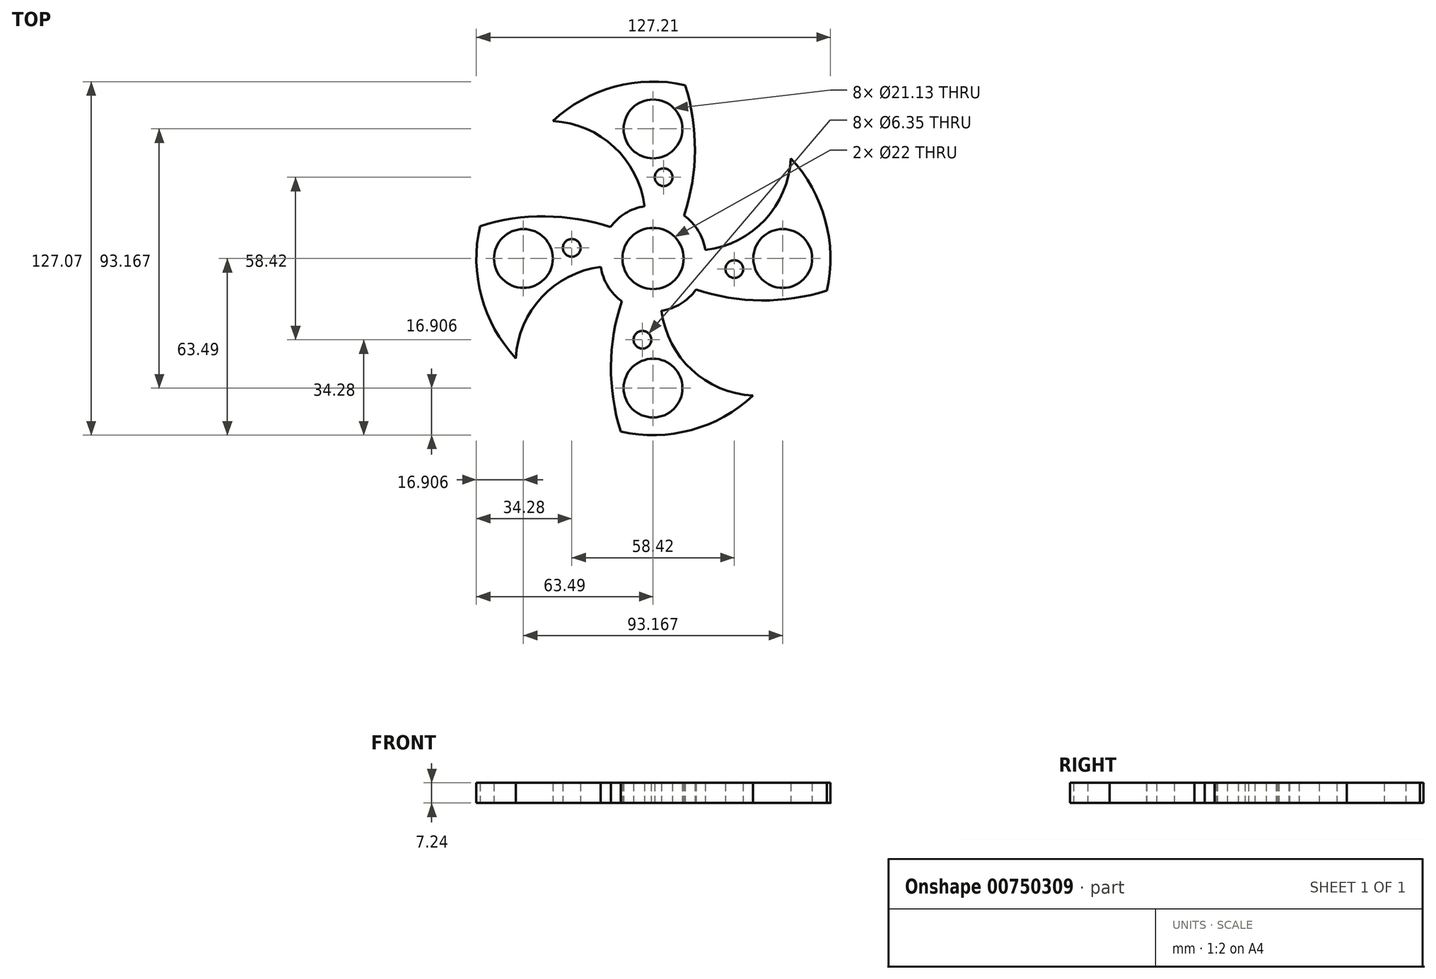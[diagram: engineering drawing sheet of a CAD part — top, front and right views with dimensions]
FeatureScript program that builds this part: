
annotation { "Feature Type Name" : "Feature", "Feature Type Description" : "" }
export const myFeature = defineFeature(function(context is Context, id is Id, definition is map)
    precondition{}
    {
        {
            var Q0;
            Q0=qCreatedBy(makeId("Top.planeOp"),FACE);
            var sketch = newSketch(context, id + "F0", { "sketchPlane" : qUnion([Q0])});
            skCircle(sketch, "E0", {"center": v(0, 0) * mm, "radius": 11 * mm});
            skLineSegment(sketch, "E1", {"start": v(0, 81.88) * mm, "end": v(0, -76.38) * mm, "construction": true});
            skLineSegment(sketch, "E2", {"start": v(-80.48, 0) * mm, "end": v(91.47, 0) * mm, "construction": true});
            skCircle(sketch, "E3", {"center": v(-46.58, 0) * mm, "radius": 10.57 * mm});
            skCircle(sketch, "E4", {"center": v(46.58, 0) * mm, "radius": 10.57 * mm});
            skCircle(sketch, "E5", {"center": v(0, 46.58) * mm, "radius": 10.57 * mm});
            skCircle(sketch, "E6", {"center": v(0, -46.58) * mm, "radius": 10.57 * mm});
            skCircle(sketch, "E7", {"center": v(0, 0) * mm, "radius": 63.5 * mm, "construction": true});
            skArc(sketch, "E8", {"start": v(18.8, 3.02) * mm, "mid": v(40.2, 13.9) * mm, "end": v(49.5, 36.02) * mm});
            skArc(sketch, "E9", {"start": v(62.44, -11.57) * mm, "mid": v(61.88, 13.83) * mm, "end": v(49.5, 36.02) * mm});
            skArc(sketch, "E10", {"start": v(15.45, -11.15) * mm, "mid": v(38.9, -15.07) * mm, "end": v(62.44, -11.57) * mm});
            skArc(sketch, "E11", {"start": v(-3.05, 10.55) * mm, "mid": v(-3.05, 10.56) * mm, "end": v(-3.05, 10.57) * mm});
            skArc(sketch, "E12", {"start": v(11.54, 62.3) * mm, "mid": v(-13.82, 61.74) * mm, "end": v(-35.97, 49.4) * mm});
            skArc(sketch, "E13", {"start": v(11.17, 15.43) * mm, "mid": v(15.05, 38.83) * mm, "end": v(11.54, 62.3) * mm});
            skCircle(sketch, "E14", {"center": v(29.21, -3.81) * mm, "radius": 3.18 * mm});
            skArc(sketch, "E15", {"start": v(2.97, -10.46) * mm, "mid": v(2.96, -10.53) * mm, "end": v(2.95, -10.6) * mm});
            skArc(sketch, "E16", {"start": v(-11.63, -62.2) * mm, "mid": v(13.73, -61.65) * mm, "end": v(35.89, -49.3) * mm});
            skArc(sketch, "E17", {"start": v(-11.26, -15.37) * mm, "mid": v(-15.13, -38.76) * mm, "end": v(-11.63, -62.2) * mm});
            skCircle(sketch, "E18", {"center": v(-3.8, -29.21) * mm, "radius": 3.18 * mm});
            skCircle(sketch, "E19", {"center": v(-29.21, 3.81) * mm, "radius": 3.18 * mm});
            skCircle(sketch, "E20", {"center": v(3.81, 29.21) * mm, "radius": 3.18 * mm});
            skArc(sketch, "E21", {"start": v(-10.45, -2.96) * mm, "mid": v(-10.52, -2.95) * mm, "end": v(-10.6, -2.94) * mm});
            skArc(sketch, "E22", {"start": v(-62.2, 11.63) * mm, "mid": v(-61.65, -13.72) * mm, "end": v(-49.3, -35.88) * mm});
            skArc(sketch, "E23", {"start": v(-15.36, 11.27) * mm, "mid": v(-38.75, 15.14) * mm, "end": v(-62.2, 11.63) * mm});
            skCircle(sketch, "E24", {"center": v(0, 0) * mm, "radius": 19.05 * mm});
            skArc(sketch, "E25.trimOffspring", {"start": v(-3.09, 18.8) * mm, "mid": v(-13.96, 40.08) * mm, "end": v(-35.97, 49.4) * mm});
            skArc(sketch, "E26.trimOffspring", {"start": v(3.02, -18.8) * mm, "mid": v(13.91, -40.02) * mm, "end": v(35.89, -49.3) * mm});
            skArc(sketch, "E27.trimOffspring", {"start": v(-18.81, -3.01) * mm, "mid": v(-40.02, -13.9) * mm, "end": v(-49.3, -35.88) * mm});
            skSolve(sketch);
        }
        {
            var Q0;
            {var subQ0=sQuery(id+"F0.wireOp",EDGE,"E12");Q0=makeQuery(id+"F0.imprint","IMPRINT",FACE,{"disambiguationData":[TD([[makeQuery(id+"F0.imprint","IMPRINT",EDGE,{"derivedFrom":subQ0}),1.0]])]});}
            var Q1;
            {var subQ0=sQuery(id+"F0.wireOp",EDGE,"E8");var subQ1=sQuery(id+"F0.wireOp",EDGE,"E0");var subQ2=makeQuery(id+"F0.imprint","INTERSECT",VERTEX,{"derivedFrom":[subQ1,subQ0]});Q1=makeQuery(id+"F0.imprint","IMPRINT",FACE,{"disambiguationData":[TD([[makeQuery(id+"F0.imprint","IMPRINT",EDGE,{"disambiguationData":[TD([[subQ2,-1.0]])],"derivedFrom":subQ1}),-1.0]])]});}
            var Q2;
            {var subQ0=sQuery(id+"F0.wireOp",EDGE,"E13");var subQ1=sQuery(id+"F0.wireOp",EDGE,"E0");var subQ2=makeQuery(id+"F0.imprint","INTERSECT",VERTEX,{"derivedFrom":[subQ1,subQ0]});Q2=makeQuery(id+"F0.imprint","IMPRINT",FACE,{"disambiguationData":[TD([[makeQuery(id+"F0.imprint","IMPRINT",EDGE,{"disambiguationData":[TD([[subQ2,-1.0]])],"derivedFrom":subQ1}),-1.0]])]});}
            var Q3;
            {var subQ0=sQuery(id+"F0.wireOp",EDGE,"E23");var subQ1=sQuery(id+"F0.wireOp",EDGE,"E0");var subQ2=makeQuery(id+"F0.imprint","INTERSECT",VERTEX,{"derivedFrom":[subQ1,subQ0]});Q3=makeQuery(id+"F0.imprint","IMPRINT",FACE,{"disambiguationData":[TD([[makeQuery(id+"F0.imprint","IMPRINT",EDGE,{"disambiguationData":[TD([[subQ2,1.0]])],"derivedFrom":subQ1}),-1.0]])]});}
            var Q4;
            {var subQ0=sQuery(id+"F0.wireOp",EDGE,"E23");var subQ1=sQuery(id+"F0.wireOp",EDGE,"E0");var subQ2=makeQuery(id+"F0.imprint","INTERSECT",VERTEX,{"derivedFrom":[subQ1,subQ0]});Q4=makeQuery(id+"F0.imprint","IMPRINT",FACE,{"disambiguationData":[TD([[makeQuery(id+"F0.imprint","IMPRINT",EDGE,{"disambiguationData":[TD([[subQ2,-1.0]])],"derivedFrom":subQ1}),-1.0]])]});}
            var Q5;
            {var subQ0=sQuery(id+"F0.wireOp",EDGE,"E17");var subQ1=sQuery(id+"F0.wireOp",EDGE,"E0");var subQ2=makeQuery(id+"F0.imprint","INTERSECT",VERTEX,{"derivedFrom":[subQ1,subQ0]});Q5=makeQuery(id+"F0.imprint","IMPRINT",FACE,{"disambiguationData":[TD([[makeQuery(id+"F0.imprint","IMPRINT",EDGE,{"disambiguationData":[TD([[subQ2,1.0]])],"derivedFrom":subQ1}),-1.0]])]});}
            var Q6;
            {var subQ0=sQuery(id+"F0.wireOp",EDGE,"E17");var subQ1=sQuery(id+"F0.wireOp",EDGE,"E0");var subQ2=makeQuery(id+"F0.imprint","INTERSECT",VERTEX,{"derivedFrom":[subQ1,subQ0]});Q6=makeQuery(id+"F0.imprint","IMPRINT",FACE,{"disambiguationData":[TD([[makeQuery(id+"F0.imprint","IMPRINT",EDGE,{"disambiguationData":[TD([[subQ2,-1.0]])],"derivedFrom":subQ1}),-1.0]])]});}
            var Q7;
            {var subQ0=sQuery(id+"F0.wireOp",EDGE,"E10");var subQ1=sQuery(id+"F0.wireOp",EDGE,"E0");var subQ2=makeQuery(id+"F0.imprint","INTERSECT",VERTEX,{"derivedFrom":[subQ1,subQ0]});Q7=makeQuery(id+"F0.imprint","IMPRINT",FACE,{"disambiguationData":[TD([[makeQuery(id+"F0.imprint","IMPRINT",EDGE,{"disambiguationData":[TD([[subQ2,1.0]])],"derivedFrom":subQ1}),-1.0]])]});}
            var Q8;
            {var subQ0=sQuery(id+"F0.wireOp",EDGE,"E8");var subQ1=sQuery(id+"F0.wireOp",EDGE,"E0");var subQ2=makeQuery(id+"F0.imprint","INTERSECT",VERTEX,{"derivedFrom":[subQ1,subQ0]});Q8=makeQuery(id+"F0.imprint","IMPRINT",FACE,{"disambiguationData":[TD([[makeQuery(id+"F0.imprint","IMPRINT",EDGE,{"disambiguationData":[TD([[subQ2,1.0]])],"derivedFrom":subQ1}),-1.0]])]});}
            var Q9;
            Q9=makeQuery(id+"F0.imprint","IMPRINT",FACE,{"disambiguationData":[TD([[makeQuery(id+"F0.imprint","IMPRINT",EDGE,{"derivedFrom":sQuery(id+"F0.wireOp",EDGE,"E4")}),-1.0]])]});
            var Q10;
            {var subQ0=sQuery(id+"F0.wireOp",EDGE,"E16");Q10=makeQuery(id+"F0.imprint","IMPRINT",FACE,{"disambiguationData":[TD([[makeQuery(id+"F0.imprint","IMPRINT",EDGE,{"derivedFrom":subQ0}),1.0]])]});}
            var Q11;
            Q11=makeQuery(id+"F0.imprint","IMPRINT",FACE,{"disambiguationData":[TD([[makeQuery(id+"F0.imprint","IMPRINT",EDGE,{"derivedFrom":sQuery(id+"F0.wireOp",EDGE,"E19")}),-1.0]])]});
            var Q12;
            {var subQ4=sQuery(id+"F0.wireOp",EDGE,"E0");var subQ5=makeQuery(id+"F0.imprint","IMPRINT",VERTEX,{"disambiguationData":[OD(0.0)],"derivedFrom":subQ4});Q12=makeQuery(id+"F0.imprint","IMPRINT",FACE,{"disambiguationData":[TD([[makeQuery(id+"F0.imprint","IMPRINT",EDGE,{"disambiguationData":[TD([[subQ5,-1.0]])],"derivedFrom":subQ4}),-1.0]])]});}
            extrude(context, id + "F1", {"entities" : qUnion([Q0, Q1, Q2, Q3, Q4, Q5, Q6, Q7, Q8, Q9, Q10, Q11, Q12]), "depth" : 7.24 * mm, "offsetDistance" : 25.4 * mm});
        }
    });
